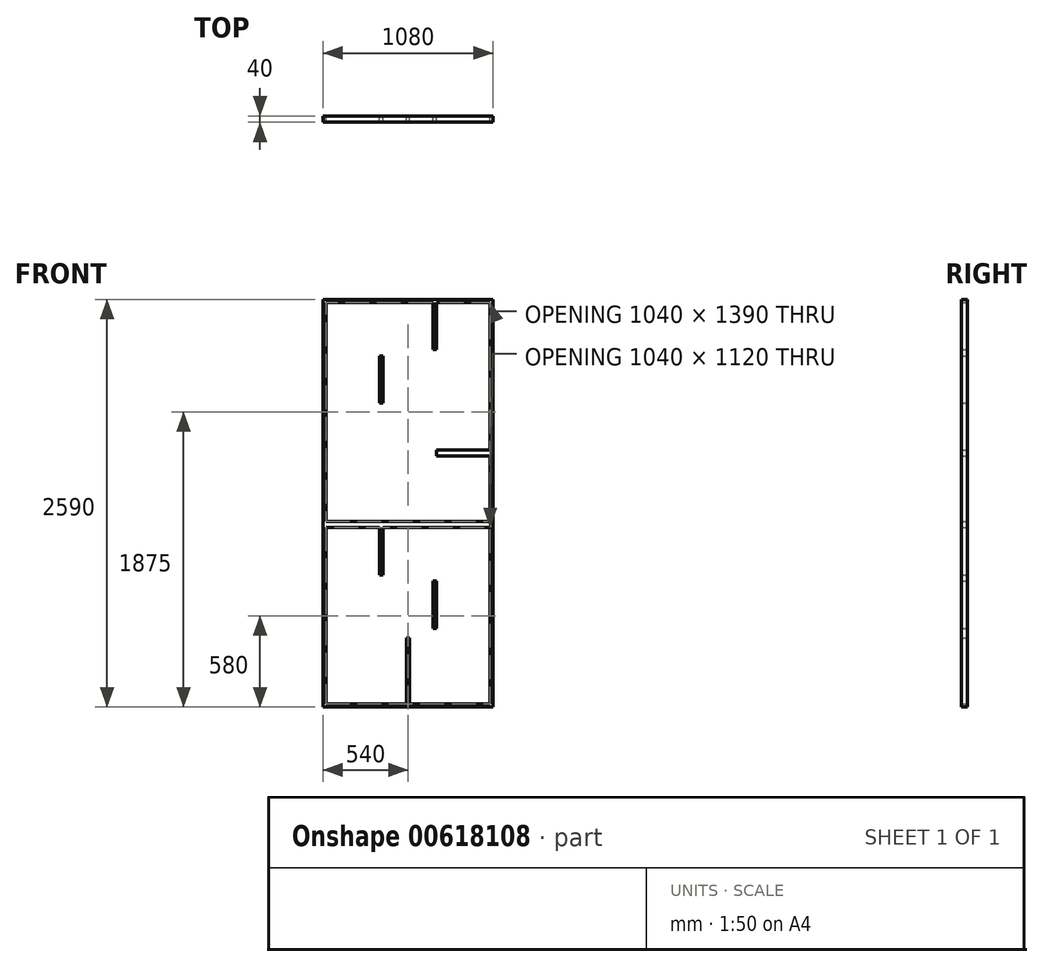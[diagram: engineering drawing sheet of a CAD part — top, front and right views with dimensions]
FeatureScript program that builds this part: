
annotation { "Feature Type Name" : "Feature", "Feature Type Description" : "" }
export const myFeature = defineFeature(function(context is Context, id is Id, definition is map)
    precondition{}
    {
        {
            var Q0;
            Q0=qCreatedBy(makeId("Front.planeOp"),FACE);
            var sketch = newSketch(context, id + "F0", { "sketchPlane" : qUnion([Q0])});
            skLineSegment(sketch, "E0.bottom", {"start": v(540, -1295) * mm, "end": v(-540, -1295) * mm});
            skLineSegment(sketch, "E0.top", {"start": v(540, 1295) * mm, "end": v(-540, 1295) * mm});
            skLineSegment(sketch, "E0.left", {"start": v(540, -1295) * mm, "end": v(540, 1295) * mm});
            skLineSegment(sketch, "E0.right", {"start": v(-540, -1295) * mm, "end": v(-540, 1295) * mm});
            skPoint(sketch, "E0.middle", {"position": v(0, 0) * mm});
            skLineSegment(sketch, "E1.bottom", {"start": v(520, -1275) * mm, "end": v(-520, -1275) * mm});
            skLineSegment(sketch, "E1.top", {"start": v(520, 1275) * mm, "end": v(-520, 1275) * mm});
            skLineSegment(sketch, "E1.left", {"start": v(520, -1275) * mm, "end": v(520, 1275) * mm});
            skLineSegment(sketch, "E1.right", {"start": v(-520, -1275) * mm, "end": v(-520, 1275) * mm});
            skLineSegment(sketch, "E2", {"start": v(-520, 975) * mm, "end": v(520, 975) * mm});
            skLineSegment(sketch, "E3", {"start": v(520, 975) * mm, "end": v(520, 935) * mm});
            skLineSegment(sketch, "E4", {"start": v(520, 935) * mm, "end": v(-520, 935) * mm});
            skLineSegment(sketch, "E5", {"start": v(-520, 935) * mm, "end": v(-520, 975) * mm});
            skLineSegment(sketch, "E6", {"start": v(-520, 635) * mm, "end": v(520, 635) * mm});
            skLineSegment(sketch, "E7", {"start": v(520, 635) * mm, "end": v(520, 595) * mm});
            skLineSegment(sketch, "E8", {"start": v(520, 595) * mm, "end": v(-520, 595) * mm});
            skLineSegment(sketch, "E9", {"start": v(-520, 595) * mm, "end": v(-520, 635) * mm});
            skLineSegment(sketch, "E10", {"start": v(-520, -855) * mm, "end": v(520, -855) * mm});
            skLineSegment(sketch, "E11", {"start": v(520, -855) * mm, "end": v(520, -795) * mm});
            skLineSegment(sketch, "E12", {"start": v(520, -795) * mm, "end": v(-520, -795) * mm});
            skLineSegment(sketch, "E13", {"start": v(-520, -795) * mm, "end": v(-520, -855) * mm});
            skLineSegment(sketch, "E14", {"start": v(-520, -455) * mm, "end": v(520, -455) * mm});
            skLineSegment(sketch, "E15", {"start": v(520, -455) * mm, "end": v(520, -495) * mm});
            skLineSegment(sketch, "E16", {"start": v(520, -495) * mm, "end": v(-520, -495) * mm});
            skLineSegment(sketch, "E17", {"start": v(-520, -155) * mm, "end": v(520, -155) * mm});
            skLineSegment(sketch, "E18", {"start": v(-520, -115) * mm, "end": v(520, -115) * mm});
            skLineSegment(sketch, "E19", {"start": v(160, 595) * mm, "end": v(160, -115) * mm});
            skLineSegment(sketch, "E20", {"start": v(180, 595) * mm, "end": v(180, -115) * mm});
            skLineSegment(sketch, "E21", {"start": v(160, 80) * mm, "end": v(160, 40) * mm});
            skLineSegment(sketch, "E22", {"start": v(180, 299.33) * mm, "end": v(520, 299.33) * mm});
            skLineSegment(sketch, "E23", {"start": v(520, 299.33) * mm, "end": v(520, 339.33) * mm});
            skLineSegment(sketch, "E24", {"start": v(520, 339.33) * mm, "end": v(180, 339.33) * mm});
            skLineSegment(sketch, "E25", {"start": v(-10, -855) * mm, "end": v(-10, -1275) * mm});
            skLineSegment(sketch, "E26", {"start": v(-10, -1275) * mm, "end": v(10, -1275) * mm});
            skLineSegment(sketch, "E27", {"start": v(10, -1275) * mm, "end": v(10, -855) * mm});
            skLineSegment(sketch, "E28", {"start": v(160, 975) * mm, "end": v(160, 1275) * mm});
            skLineSegment(sketch, "E29", {"start": v(160, 1275) * mm, "end": v(180, 1275) * mm});
            skLineSegment(sketch, "E30", {"start": v(180, 1275) * mm, "end": v(180, 975) * mm});
            skLineSegment(sketch, "E31", {"start": v(-180, 935) * mm, "end": v(-180, 635) * mm});
            skLineSegment(sketch, "E32", {"start": v(-180, 635) * mm, "end": v(-160, 635) * mm});
            skLineSegment(sketch, "E33", {"start": v(-160, 635) * mm, "end": v(-160, 935) * mm});
            skLineSegment(sketch, "E34", {"start": v(-180, -155) * mm, "end": v(-180, -455) * mm});
            skLineSegment(sketch, "E35", {"start": v(-180, -455) * mm, "end": v(-160, -455) * mm});
            skLineSegment(sketch, "E36", {"start": v(-160, -455) * mm, "end": v(-160, -155) * mm});
            skLineSegment(sketch, "E37", {"start": v(160, -495) * mm, "end": v(160, -795) * mm});
            skLineSegment(sketch, "E38", {"start": v(160, -795) * mm, "end": v(180, -795) * mm});
            skLineSegment(sketch, "E39", {"start": v(180, -795) * mm, "end": v(180, -495) * mm});
            skSolve(sketch);
        }
        {
            var Q0;
            Q0=makeQuery(id+"F0.imprint","IMPRINT",FACE,{"disambiguationData":[TD([[makeQuery(id+"F0.imprint","IMPRINT",EDGE,{"derivedFrom":sQuery(id+"F0.wireOp",EDGE,"E0.bottom")}),-1.0]])]});
            var Q1;
            {var subQ0=sQuery(id+"F0.wireOp",EDGE,"E28");Q1=makeQuery(id+"F0.imprint","IMPRINT",FACE,{"disambiguationData":[TD([[makeQuery(id+"F0.imprint","IMPRINT",EDGE,{"derivedFrom":subQ0}),-1.0]])]});}
            var Q2;
            {var subQ0=sQuery(id+"F0.wireOp",EDGE,"E3");Q2=makeQuery(id+"F0.imprint","IMPRINT",FACE,{"disambiguationData":[TD([[makeQuery(id+"F0.imprint","IMPRINT",EDGE,{"derivedFrom":subQ0}),-1.0]])]});}
            var Q3;
            {var subQ0=sQuery(id+"F0.wireOp",EDGE,"E31");Q3=makeQuery(id+"F0.imprint","IMPRINT",FACE,{"disambiguationData":[TD([[makeQuery(id+"F0.imprint","IMPRINT",EDGE,{"derivedFrom":subQ0}),1.0]])]});}
            var Q4;
            {var subQ1=sQuery(id+"F0.wireOp",EDGE,"E7");Q4=makeQuery(id+"F0.imprint","IMPRINT",FACE,{"disambiguationData":[TD([[makeQuery(id+"F0.imprint","IMPRINT",EDGE,{"derivedFrom":subQ1}),-1.0]])]});}
            var Q5;
            {var subQ3=sQuery(id+"F0.wireOp",EDGE,"E21");Q5=makeQuery(id+"F0.imprint","IMPRINT",FACE,{"disambiguationData":[TD([[makeQuery(id+"F0.imprint","IMPRINT",EDGE,{"derivedFrom":subQ3}),1.0]])]});}
            var Q6;
            {var subQ0=sQuery(id+"F0.wireOp",EDGE,"E22");Q6=makeQuery(id+"F0.imprint","IMPRINT",FACE,{"disambiguationData":[TD([[makeQuery(id+"F0.imprint","IMPRINT",EDGE,{"derivedFrom":subQ0}),1.0]])]});}
            var Q7;
            {var subQ0=sQuery(id+"F0.wireOp",EDGE,"vNZAfOef-FLmt-84hy-Cmou-KtLhwa7gYjMc");Q7=makeQuery(id+"F0.imprint","IMPRINT",FACE,{"disambiguationData":[TD([[makeQuery(id+"F0.imprint","IMPRINT",EDGE,{"derivedFrom":subQ0}),-1.0]])]});}
            var Q8;
            {var subQ0=sQuery(id+"F0.wireOp",EDGE,"E17");var subQ5=sQuery(id+"F0.wireOp",EDGE,"E1.left");var subQ6=makeQuery(id+"F0.imprint","INTERSECT",VERTEX,{"derivedFrom":[subQ5,subQ0]});Q8=makeQuery(id+"F0.imprint","IMPRINT",FACE,{"disambiguationData":[TD([[makeQuery(id+"F0.imprint","IMPRINT",EDGE,{"disambiguationData":[TD([[subQ6,-1.0]])],"derivedFrom":subQ5}),1.0]])]});}
            var Q9;
            {var subQ0=sQuery(id+"F0.wireOp",EDGE,"E34");Q9=makeQuery(id+"F0.imprint","IMPRINT",FACE,{"disambiguationData":[TD([[makeQuery(id+"F0.imprint","IMPRINT",EDGE,{"derivedFrom":subQ0}),1.0]])]});}
            var Q10;
            {var subQ0=sQuery(id+"F0.wireOp",EDGE,"E15");Q10=makeQuery(id+"F0.imprint","IMPRINT",FACE,{"disambiguationData":[TD([[makeQuery(id+"F0.imprint","IMPRINT",EDGE,{"derivedFrom":subQ0}),-1.0]])]});}
            var Q11;
            {var subQ0=sQuery(id+"F0.wireOp",EDGE,"E37");Q11=makeQuery(id+"F0.imprint","IMPRINT",FACE,{"disambiguationData":[TD([[makeQuery(id+"F0.imprint","IMPRINT",EDGE,{"derivedFrom":subQ0}),1.0]])]});}
            var Q12;
            {var subQ0=sQuery(id+"F0.wireOp",EDGE,"E11");Q12=makeQuery(id+"F0.imprint","IMPRINT",FACE,{"disambiguationData":[TD([[makeQuery(id+"F0.imprint","IMPRINT",EDGE,{"derivedFrom":subQ0}),1.0]])]});}
            var Q13;
            {var subQ0=sQuery(id+"F0.wireOp",EDGE,"E25");Q13=makeQuery(id+"F0.imprint","IMPRINT",FACE,{"disambiguationData":[TD([[makeQuery(id+"F0.imprint","IMPRINT",EDGE,{"derivedFrom":subQ0}),1.0]])]});}
            extrude(context, id + "F1", {"entities" : qUnion([Q0, Q1, Q2, Q3, Q4, Q5, Q6, Q7, Q8, Q9, Q10, Q11, Q12, Q13]), "depth" : 40 * mm, "offsetDistance" : 25 * mm});
        }
    });
